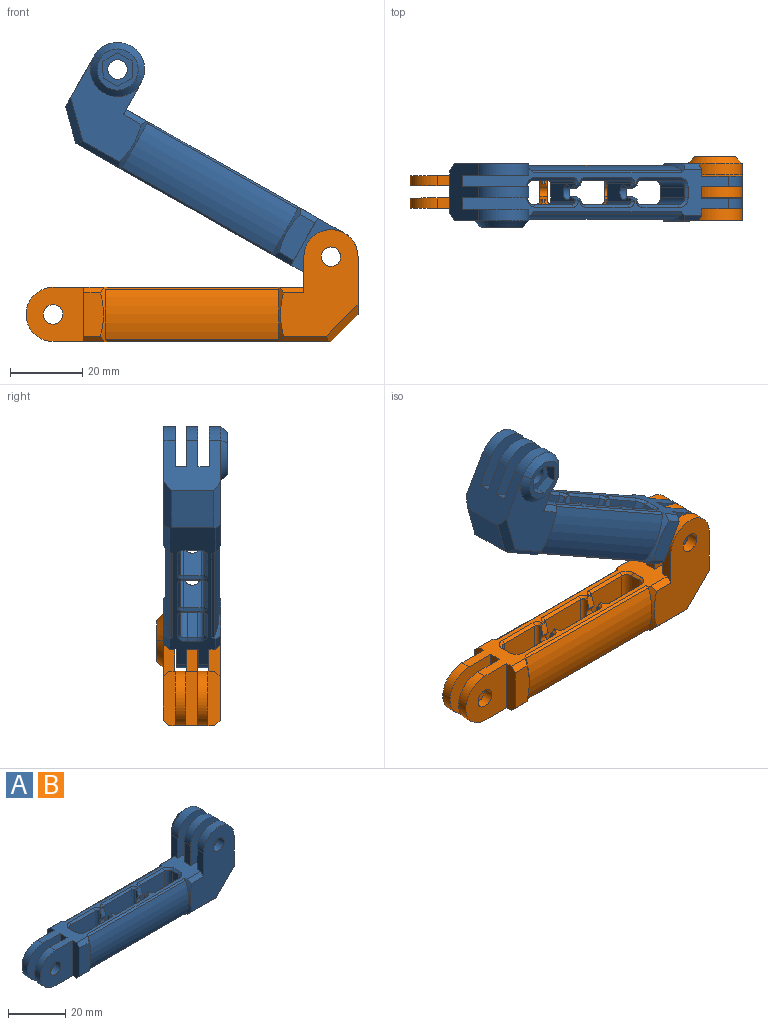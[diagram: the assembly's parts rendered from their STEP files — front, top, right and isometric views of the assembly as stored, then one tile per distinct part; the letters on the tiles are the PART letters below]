
ASSEMBLY  parts=2 mates=1
PART A: 144 faces, bbox 92.1x18.6x31.8 mm
  f0: plane 15x3.4mm, normal (-1,0,0), area 51mm2, adj f3,f4,f111,f116
  f1: plane 15x3.4mm, normal (-1,0,0), area 48.8mm2, adj f3,f4,f5,f15,f16,f115
  f2: plane 13.5x12mm, normal (0,1,0), area 162mm2, adj f18,f19,f22,f30
  f3: plane 84.51x12.81mm, normal (0,0,1), area 414.4mm2, adj f0,f1,f6,f11,f14,f16,f28,f29
  f4: plane 77.01x12.81mm, normal (0,0,-1), area 420mm2, adj f0,f1,f6,f14,f15,f20,f21,f22
  f5: plane 12.01x5.5mm, normal (0,-1,0), area 62.4mm2, adj f1,f14,f15,f16
  f6: plane 15x3.4mm, normal (-1,0,0), area 48.7mm2, adj f3,f4,f39,f44,f45,f112
  f7: cylinder r=19.5mm len=48mm, axis (-1,0,0), area 689.4mm2, adj f14,f36,f37,f70
  f8: plane 13.5x2.8mm, normal (1,0,0), area 37.8mm2, adj f19,f20,f32,f48
  f9: plane 14x13.5mm, normal (0,1,0), area 189mm2, adj f17,f25,f33,f73
  f10: cylinder r=2.1mm len=4.2mm, axis (1,0,0), area 21.3mm2, adj f11,f12,f13,f42
  f11: plane 3.28x2mm, normal (0,0.96,0.29), area 6.3mm2, adj f3,f10,f12,f13,f28,f35
  f12: plane 13.5x4.8mm, normal (-1,0,0), area 43.5mm2, adj f10,f11,f18,f24,f28,f42,f47,f54
  f13: plane 13.5x4.8mm, normal (1,0,0), area 43.5mm2, adj f10,f11,f17,f27,f35,f42,f46,f60
  f14: cone r=21.5mm half-angle=45deg, axis (-1,0,0), area 18.3mm2, adj f3,f4,f5,f7,f15,f16,f36,f37
  f15: plane 5.62x1.58mm, normal (0,-0.71,-0.71), area 10.8mm2, adj f1,f4,f5,f14
  f16: plane 5.62x1.58mm, normal (0,-0.71,0.71), area 10.8mm2, adj f1,f3,f5,f14
  f17: cylinder r=1mm len=13.5mm, axis (0,0,1), area 21.2mm2, adj f9,f13,f26,f34
  f18: cylinder r=1mm len=13.5mm, axis (0,0,-1), area 21.2mm2, adj f2,f12,f23,f29
  f19: cylinder r=2mm len=13.5mm, axis (0,0,-1), area 42.4mm2, adj f2,f8,f21,f31
  f20: plane 2.8x0.75mm, normal (0.71,0,-0.71), area 3mm2, adj f4,f8,f21,f49
  f21: cone r=2.75mm half-angle=45deg, axis (0,0,-1), area 4mm2, adj f4,f19,f20,f22
  f22: plane 12x0.75mm, normal (0,0.71,-0.71), area 12.7mm2, adj f2,f4,f21,f23
  f23: cone r=1.75mm half-angle=45deg, axis (0,0,-1), area 2.3mm2, adj f4,f18,f22,f24
  f24: plane 4.8x0.75mm, normal (-0.71,0,-0.71), area 5.1mm2, adj f4,f12,f23,f51
  f25: plane 14x0.75mm, normal (0,0.71,-0.71), area 14.8mm2, adj f4,f9,f26,f81
  f26: cone r=1.75mm half-angle=45deg, axis (0,0,-1), area 2.3mm2, adj f4,f17,f25,f27
  f27: plane 4.8x0.75mm, normal (0.71,0,-0.71), area 5.1mm2, adj f4,f13,f26,f53
  f28: plane 0.75x0.75mm, normal (-0.71,0,0.71), area 0.3mm2, adj f3,f11,f12,f29
  f29: cone r=1.75mm half-angle=45deg, axis (0,0,1), area 2.3mm2, adj f3,f18,f28,f30
  f30: plane 12x0.75mm, normal (0,0.71,0.71), area 12.7mm2, adj f2,f3,f29,f31
  f31: cone r=2.75mm half-angle=45deg, axis (0,0,1), area 4mm2, adj f3,f19,f30,f32
  f32: plane 2.8x0.75mm, normal (0.71,0,0.71), area 3mm2, adj f3,f8,f31,f57
  f33: plane 14x0.75mm, normal (0,0.71,0.71), area 14.8mm2, adj f3,f9,f34,f88
  f34: cone r=1.75mm half-angle=45deg, axis (0,0,1), area 2.3mm2, adj f3,f17,f33,f35
  f35: plane 0.75x0.75mm, normal (0.71,0,0.71), area 0.3mm2, adj f3,f11,f13,f34
  f36: plane 48.01x0.71mm, normal (0,-0.57,-0.82), area 40.3mm2, adj f4,f7,f14,f70
  f37: plane 48.01x0.71mm, normal (0,-0.57,0.82), area 40.3mm2, adj f3,f7,f14,f70
  f38: plane 13.5x12mm, normal (0,-1,0), area 162mm2, adj f47,f48,f50,f56
  f39: plane 12.01x5.5mm, normal (0,1,0), area 62.4mm2, adj f6,f43,f44,f45
  f40: cylinder r=19.5mm len=48mm, axis (-1,0,0), area 689.4mm2, adj f43,f61,f62,f93
  f41: plane 14x13.5mm, normal (0,-1,0), area 189mm2, adj f46,f52,f58,f96
  f42: plane 3.28x2mm, normal (0,-0.96,0.29), area 6.3mm2, adj f3,f10,f12,f13,f54,f60
  f43: cone r=21.5mm half-angle=45deg, axis (-1,0,0), area 18.3mm2, adj f3,f4,f39,f40,f44,f45,f61,f62
  f44: plane 5.62x1.58mm, normal (0,0.71,-0.71), area 10.8mm2, adj f4,f6,f39,f43
  f45: plane 5.62x1.58mm, normal (0,0.71,0.71), area 10.8mm2, adj f3,f6,f39,f43
  f46: cylinder r=1mm len=13.5mm, axis (0,0,1), area 21.2mm2, adj f13,f41,f53,f59
  f47: cylinder r=1mm len=13.5mm, axis (0,0,-1), area 21.2mm2, adj f12,f38,f51,f55
  f48: cylinder r=2mm len=13.5mm, axis (0,0,-1), area 42.4mm2, adj f8,f38,f49,f57
  f49: cone r=2.75mm half-angle=45deg, axis (0,0,-1), area 4mm2, adj f4,f20,f48,f50
  f50: plane 12x0.75mm, normal (0,-0.71,-0.71), area 12.7mm2, adj f4,f38,f49,f51
  f51: cone r=1.75mm half-angle=45deg, axis (0,0,-1), area 2.3mm2, adj f4,f24,f47,f50
  f52: plane 14x0.75mm, normal (0,-0.71,-0.71), area 14.8mm2, adj f4,f41,f53,f102
  f53: cone r=1.75mm half-angle=45deg, axis (0,0,-1), area 2.3mm2, adj f4,f27,f46,f52
  f54: plane 0.75x0.75mm, normal (-0.71,0,0.71), area 0.3mm2, adj f3,f12,f42,f55
  f55: cone r=1.75mm half-angle=45deg, axis (0,0,1), area 2.3mm2, adj f3,f47,f54,f56
  f56: plane 12x0.75mm, normal (0,-0.71,0.71), area 12.7mm2, adj f3,f38,f55,f57
  f57: cone r=2.75mm half-angle=45deg, axis (0,0,1), area 4mm2, adj f3,f32,f48,f56
  f58: plane 14x0.75mm, normal (0,-0.71,0.71), area 14.8mm2, adj f3,f41,f59,f107
  f59: cone r=1.75mm half-angle=45deg, axis (0,0,1), area 2.3mm2, adj f3,f46,f58,f60
  f60: plane 0.75x0.75mm, normal (0.71,0,0.71), area 0.3mm2, adj f3,f13,f42,f59
  f61: plane 48.01x0.71mm, normal (0,0.57,-0.82), area 40.3mm2, adj f4,f40,f43,f93
  f62: plane 48.01x0.71mm, normal (0,0.57,0.82), area 40.3mm2, adj f3,f40,f43,f93
  f63: plane 13.5x12mm, normal (0,1,0), area 162mm2, adj f74,f75,f78,f85
  f64: plane 29.5x21.5mm, normal (0,-1,0), area 430.9mm2, adj f70,f71,f72,f117,f132,f133,f134,f143
  f65: plane 13.5x2.8mm, normal (-1,0,0), area 37.8mm2, adj f75,f76,f87,f98
  f66: cylinder r=2.1mm len=4.2mm, axis (-1,0,0), area 21.3mm2, adj f67,f68,f69,f92
  f67: plane 3.28x2mm, normal (0,0.96,0.29), area 6.3mm2, adj f3,f66,f68,f69,f83,f89
  f68: plane 13.5x4.8mm, normal (1,0,0), area 43.5mm2, adj f66,f67,f74,f80,f83,f92,f97,f103
  f69: plane 13.5x4.8mm, normal (-1,0,0), area 43.5mm2, adj f66,f67,f73,f82,f89,f92,f96,f108
  f70: cone r=21.5mm half-angle=45deg, axis (1,0,0), area 18.3mm2, adj f3,f4,f7,f36,f37,f64,f71,f72
  f71: plane 13.41x1.58mm, normal (0,-0.71,-0.71), area 26.7mm2, adj f4,f64,f70,f143
  f72: plane 6.62x1.58mm, normal (0,-0.71,0.71), area 12.9mm2, adj f3,f64,f70,f134
  f73: cylinder r=1mm len=13.5mm, axis (0,0,1), area 21.2mm2, adj f9,f69,f81,f88
  f74: cylinder r=1mm len=13.5mm, axis (0,0,-1), area 21.2mm2, adj f63,f68,f79,f84
  f75: cylinder r=2mm len=13.5mm, axis (0,0,-1), area 42.4mm2, adj f63,f65,f77,f86
  f76: plane 2.8x0.75mm, normal (-0.71,0,-0.71), area 3mm2, adj f4,f65,f77,f99
  f77: cone r=2.75mm half-angle=45deg, axis (0,0,-1), area 4mm2, adj f4,f75,f76,f78
  f78: plane 12x0.75mm, normal (0,0.71,-0.71), area 12.7mm2, adj f4,f63,f77,f79
  f79: cone r=1.75mm half-angle=45deg, axis (0,0,-1), area 2.3mm2, adj f4,f74,f78,f80
  f80: plane 4.8x0.75mm, normal (0.71,0,-0.71), area 5.1mm2, adj f4,f68,f79,f101
  f81: cone r=1.75mm half-angle=45deg, axis (0,0,-1), area 2.3mm2, adj f4,f25,f73,f82
  f82: plane 4.8x0.75mm, normal (-0.71,0,-0.71), area 5.1mm2, adj f4,f69,f81,f102
  f83: plane 0.75x0.75mm, normal (0.71,0,0.71), area 0.3mm2, adj f3,f67,f68,f84
  f84: cone r=1.75mm half-angle=45deg, axis (0,0,1), area 2.3mm2, adj f3,f74,f83,f85
  f85: plane 12x0.75mm, normal (0,0.71,0.71), area 12.7mm2, adj f3,f63,f84,f86
  f86: cone r=2.75mm half-angle=45deg, axis (0,0,1), area 4mm2, adj f3,f75,f85,f87
  f87: plane 2.8x0.75mm, normal (-0.71,0,0.71), area 3mm2, adj f3,f65,f86,f106
  f88: cone r=1.75mm half-angle=45deg, axis (0,0,1), area 2.3mm2, adj f3,f33,f73,f89
  f89: plane 0.75x0.75mm, normal (-0.71,0,0.71), area 0.3mm2, adj f3,f67,f69,f88
  f90: plane 13.5x12mm, normal (0,-1,0), area 162mm2, adj f97,f98,f100,f105
  f91: plane 22.02x21.51mm, normal (0,1,0), area 277.1mm2, adj f93,f94,f95,f117,f125,f131,f142
  f92: plane 3.28x2mm, normal (0,-0.96,0.29), area 6.3mm2, adj f3,f66,f68,f69,f103,f108
  f93: cone r=21.5mm half-angle=45deg, axis (1,0,0), area 18.3mm2, adj f3,f4,f40,f61,f62,f91,f94,f95
  f94: plane 13.41x1.58mm, normal (0,0.71,-0.71), area 26.7mm2, adj f4,f91,f93,f142
  f95: plane 6.62x1.58mm, normal (0,0.71,0.71), area 12.9mm2, adj f3,f91,f93,f131
  f96: cylinder r=1mm len=13.5mm, axis (0,0,1), area 21.2mm2, adj f41,f69,f102,f107
  f97: cylinder r=1mm len=13.5mm, axis (0,0,-1), area 21.2mm2, adj f68,f90,f101,f104
  f98: cylinder r=2mm len=13.5mm, axis (0,0,-1), area 42.4mm2, adj f65,f90,f99,f106
  f99: cone r=2.75mm half-angle=45deg, axis (0,0,-1), area 4mm2, adj f4,f76,f98,f100
  f100: plane 12x0.75mm, normal (0,-0.71,-0.71), area 12.7mm2, adj f4,f90,f99,f101
  f101: cone r=1.75mm half-angle=45deg, axis (0,0,-1), area 2.3mm2, adj f4,f80,f97,f100
  f102: cone r=1.75mm half-angle=45deg, axis (0,0,-1), area 2.3mm2, adj f4,f52,f82,f96
  f103: plane 0.75x0.75mm, normal (0.71,0,0.71), area 0.3mm2, adj f3,f68,f92,f104
  f104: cone r=1.75mm half-angle=45deg, axis (0,0,1), area 2.3mm2, adj f3,f97,f103,f105
  f105: plane 12x0.75mm, normal (0,-0.71,0.71), area 12.7mm2, adj f3,f90,f104,f106
  f106: cone r=2.75mm half-angle=45deg, axis (0,0,1), area 4mm2, adj f3,f87,f98,f105
  f107: cone r=1.75mm half-angle=45deg, axis (0,0,1), area 2.3mm2, adj f3,f58,f96,f108
  f108: plane 0.75x0.75mm, normal (-0.71,0,0.71), area 0.3mm2, adj f3,f69,f92,f107
  f109: cylinder r=2.7mm len=5.4mm, axis (0,-1,0), area 47.5mm2, adj f111,f112
  f110: cylinder r=7.5mm len=15mm, axis (0,-1,0), area 66mm2, adj f3,f4,f111,f112
  f111: plane 16x15mm, normal (0,-1,0), area 193mm2, adj f0,f3,f4,f109,f110
  f112: plane 16x15mm, normal (0,1,0), area 193mm2, adj f3,f4,f6,f109,f110
  f113: cylinder r=7.5mm len=15mm, axis (0,1,0), area 66mm2, adj f3,f4,f115,f116
  f114: cylinder r=2.7mm len=5.4mm, axis (0,1,0), area 47.5mm2, adj f115,f116
  f115: plane 16x15mm, normal (0,-1,0), area 193mm2, adj f1,f3,f4,f113,f114
  f116: plane 16x15mm, normal (0,1,0), area 193mm2, adj f0,f3,f4,f113,f114
  f117: plane 16x15.8mm, normal (1,0,0), area 193.6mm2, adj f3,f64,f91,f128,f129,f133,f135,f137
  f118: plane 9.35x8.1mm, normal (0,1,0), area 33.9mm2, adj f119,f120,f121,f122,f123,f124,f130
  f119: plane 4.68x3mm, normal (0,0,-1), area 14mm2, adj f118,f120,f124,f127
  f120: plane 4.05x3mm, normal (0.87,0,-0.5), area 14mm2, adj f118,f119,f121,f127
  f121: plane 4.05x3mm, normal (0.87,0,0.5), area 14mm2, adj f118,f120,f122,f127
  f122: plane 4.68x3mm, normal (0,0,1), area 14mm2, adj f118,f121,f123,f127
  f123: plane 4.05x3mm, normal (-0.87,0,0.5), area 14mm2, adj f118,f122,f124,f127
  f124: plane 4.05x3mm, normal (-0.87,0,-0.5), area 14mm2, adj f118,f119,f123,f127
  f125: bspline ~15.01x7.5mm, area 52.8mm2, adj f91,f126,f127
  f126: cone r=5.7mm half-angle=45deg, axis (0,-1,0), area 52.8mm2, adj f125,f127,f128
  f127: plane 11.42x11.42mm, normal (0,1,0), area 45.2mm2, adj f119,f120,f121,f122,f123,f124,f125,f126
  f128: cylinder r=7.5mm len=15mm, axis (0,-1,0), area 75.4mm2, adj f117,f126,f129,f131
  f129: plane 16x15mm, normal (0,-1,0), area 193mm2, adj f3,f117,f128,f130,f131
  f130: cylinder r=2.7mm len=5.4mm, axis (0,-1,0), area 33.9mm2, adj f118,f129
  f131: plane 10x3.2mm, normal (-1,0,0), area 28.3mm2, adj f3,f91,f95,f128,f129
  f132: cylinder r=2.7mm len=5.4mm, axis (0,1,0), area 54.3mm2, adj f64,f135
  f133: cylinder r=7.5mm len=15mm, axis (0,1,0), area 75.4mm2, adj f64,f117,f134,f135
  f134: plane 10x3.2mm, normal (-1,0,0), area 28.3mm2, adj f3,f64,f72,f133,f135
  f135: plane 16x15mm, normal (0,1,0), area 193mm2, adj f3,f117,f132,f133,f134
  f136: plane 8.5x3.1mm, normal (-1,0,0), area 26.3mm2, adj f3,f137,f139,f140
  f137: cylinder r=7.5mm len=15mm, axis (0,-1,0), area 73mm2, adj f117,f136,f139,f140
  f138: cylinder r=2.7mm len=5.4mm, axis (0,-1,0), area 52.6mm2, adj f139,f140
  f139: plane 16x15mm, normal (0,1,0), area 193mm2, adj f3,f117,f136,f137,f138
  f140: plane 16x15mm, normal (0,-1,0), area 193mm2, adj f3,f117,f136,f137,f138
  f141: plane 11.8x7.5mm, normal (0.71,0,-0.71), area 125.2mm2, adj f4,f117,f142,f143
  f142: plane 10.33x8.83mm, normal (0.5,0.71,-0.5), area 33.4mm2, adj f4,f91,f94,f117,f141
  f143: plane 10.33x8.83mm, normal (0.5,-0.71,-0.5), area 33.4mm2, adj f4,f64,f71,f117,f141
PART B: same geometry as A
PLACE A rot(axis=(0.25,0,0.97),180deg) t=(30.5,-0.64,59.89)mm
PLACE B t=(29.2,-0.44,23.95)mm fixed
MATE revolute A.f109 <-> B.f126  axis (0,-1,0) through (67.7,-5.14,47.45)mm
